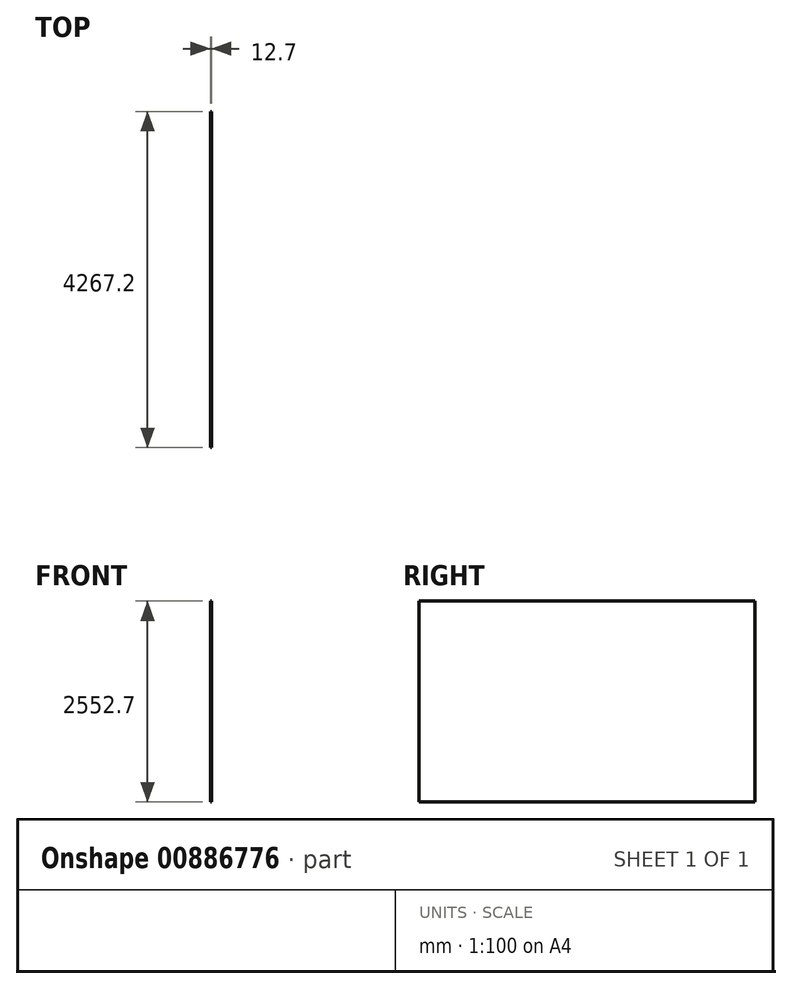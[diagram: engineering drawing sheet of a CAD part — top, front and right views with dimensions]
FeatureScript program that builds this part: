
annotation { "Feature Type Name" : "Feature", "Feature Type Description" : "" }
export const myFeature = defineFeature(function(context is Context, id is Id, definition is map)
    precondition{}
    {
        {
            var Q0;
            Q0=qCreatedBy(makeId("Right.planeOp"),FACE);
            var sketch = newSketch(context, id + "F0", { "sketchPlane" : qUnion([Q0])});
            skLineSegment(sketch, "E0.bottom", {"start": v(-2133.6, 1276.35) * mm, "end": v(2133.6, 1276.35) * mm});
            skLineSegment(sketch, "E0.top", {"start": v(-2133.6, -1276.35) * mm, "end": v(2133.6, -1276.35) * mm});
            skLineSegment(sketch, "E0.left", {"start": v(-2133.6, 1276.35) * mm, "end": v(-2133.6, -1276.35) * mm});
            skLineSegment(sketch, "E0.right", {"start": v(2133.6, 1276.35) * mm, "end": v(2133.6, -1276.35) * mm});
            skPoint(sketch, "E0.middle", {"position": v(0, 0) * mm});
            skSolve(sketch);
        }
        {
            var Q0;
            Q0 = qSketchRegion(id + "F0", true);
            extrude(context, id + "F1", {"entities" : qUnion([Q0]), "depth" : 12.7 * mm, "offsetDistance" : 25.4 * mm});
        }
    });
